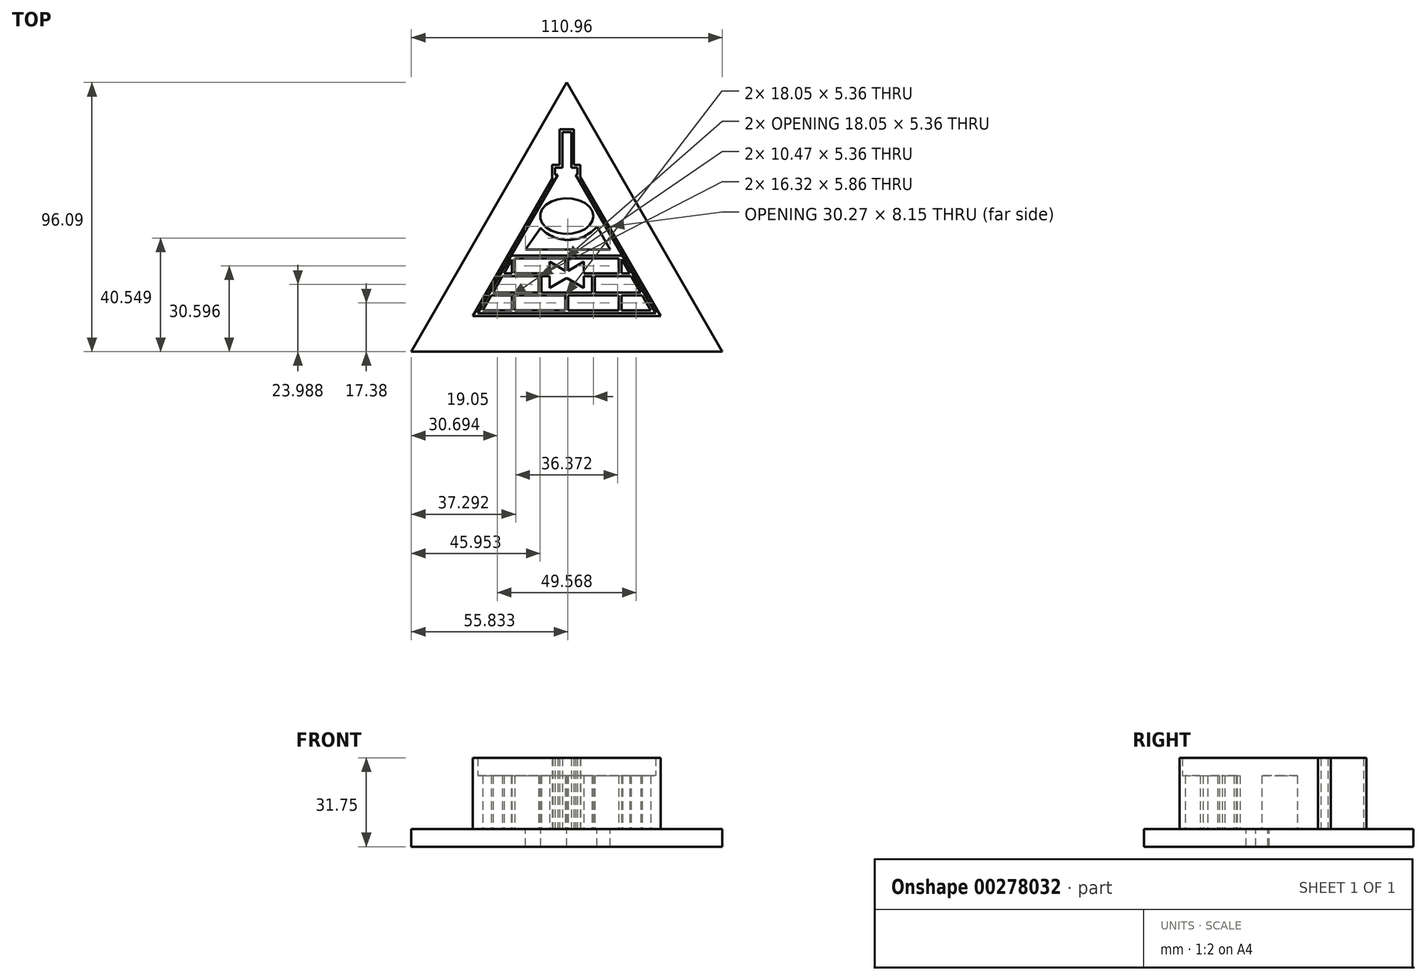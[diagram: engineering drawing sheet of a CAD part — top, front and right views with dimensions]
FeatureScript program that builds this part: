
annotation { "Feature Type Name" : "Feature", "Feature Type Description" : "" }
export const myFeature = defineFeature(function(context is Context, id is Id, definition is map)
    precondition{}
    {
        {
            var Q0;
            Q0=qCreatedBy(makeId("Top.planeOp"),FACE);
            var sketch = newSketch(context, id + "F0", { "sketchPlane" : qUnion([Q0])});
            skLineSegment(sketch, "E0", {"start": v(-57.59, 40.25) * mm, "end": v(-86.1, -9.14) * mm});
            skLineSegment(sketch, "E1", {"start": v(-86.1, -9.14) * mm, "end": v(-22.6, -9.14) * mm});
            skLineSegment(sketch, "E2", {"start": v(-22.6, -9.14) * mm, "end": v(-51.12, 40.25) * mm});
            skEllipse(sketch, "E3", {"center": v(-54.35, 25.53) * mm, "majorRadius": 6.35 * mm, "minorRadius": 9.53 * mm, "majorAxis": v(0, -1)});
            skPoint(sketch, "E4.startSnap0", {"position": v(-63.88, 25.53) * mm});
            skPoint(sketch, "E4.endSnap0", {"position": v(-63.88, 25.53) * mm});
            skLineSegment(sketch, "E5", {"start": v(-74.22, 11.44) * mm, "end": v(-34.48, 11.44) * mm});
            skLineSegment(sketch, "E6", {"start": v(-30.52, 4.58) * mm, "end": v(-49.3, 4.58) * mm});
            skLineSegment(sketch, "E7", {"start": v(-82.14, -2.28) * mm, "end": v(-26.56, -2.28) * mm});
            skLineSegment(sketch, "E8", {"start": v(-73.4, 11.44) * mm, "end": v(-73.4, 4.58) * mm});
            skLineSegment(sketch, "E9", {"start": v(-35.3, 11.44) * mm, "end": v(-35.3, 4.58) * mm});
            skLineSegment(sketch, "E10", {"start": v(-63.88, 4.58) * mm, "end": v(-63.88, -2.28) * mm});
            skLineSegment(sketch, "E11", {"start": v(-44.83, 4.58) * mm, "end": v(-44.83, -2.28) * mm});
            skLineSegment(sketch, "E12.trimOffspring", {"start": v(-35.3, -2.28) * mm, "end": v(-35.3, -9.14) * mm});
            skLineSegment(sketch, "E13.trimOffspring", {"start": v(-54.35, -2.28) * mm, "end": v(-54.35, -9.14) * mm});
            skLineSegment(sketch, "E14.bottom", {"start": v(-54.35, 29.34) * mm, "end": v(-54.35, 29.34) * mm});
            skLineSegment(sketch, "E14.top", {"start": v(-54.35, 21.72) * mm, "end": v(-54.35, 21.72) * mm});
            skLineSegment(sketch, "E14.left", {"start": v(-54.86, 28.84) * mm, "end": v(-54.86, 22.23) * mm});
            skLineSegment(sketch, "E14.right", {"start": v(-53.84, 28.84) * mm, "end": v(-53.84, 22.23) * mm});
            skPoint(sketch, "E15.visualSharp", {"position": v(-54.86, 29.34) * mm});
            skArc(sketch, "E15.filletArc", {"start": v(-54.35, 29.34) * mm, "mid": v(-54.71, 29.2) * mm, "end": v(-54.86, 28.84) * mm});
            skPoint(sketch, "E16.visualSharp", {"position": v(-53.84, 29.34) * mm});
            skArc(sketch, "E16.filletArc", {"start": v(-53.84, 28.84) * mm, "mid": v(-54, 29.2) * mm, "end": v(-54.35, 29.34) * mm});
            skPoint(sketch, "E17.visualSharp", {"position": v(-54.86, 21.72) * mm});
            skArc(sketch, "E17.filletArc", {"start": v(-54.86, 22.23) * mm, "mid": v(-54.71, 21.87) * mm, "end": v(-54.35, 21.72) * mm});
            skPoint(sketch, "E18.visualSharp", {"position": v(-53.84, 21.72) * mm});
            skArc(sketch, "E18.filletArc", {"start": v(-54.35, 21.72) * mm, "mid": v(-54, 21.87) * mm, "end": v(-53.84, 22.23) * mm});
            skLineSegment(sketch, "E19.trimOffspring", {"start": v(-59.41, 4.58) * mm, "end": v(-78.18, 4.58) * mm});
            skLineSegment(sketch, "E20.bottom", {"start": v(-58.55, 40.25) * mm, "end": v(-57.59, 40.25) * mm});
            skLineSegment(sketch, "E20.top", {"start": v(-58.55, 42.8) * mm, "end": v(-55.94, 42.8) * mm});
            skLineSegment(sketch, "E20.left", {"start": v(-58.55, 40.25) * mm, "end": v(-58.55, 42.8) * mm});
            skLineSegment(sketch, "E20.right", {"start": v(-50.54, 40.25) * mm, "end": v(-50.54, 42.8) * mm});
            skLineSegment(sketch, "E21.top", {"start": v(-55.94, 55.5) * mm, "end": v(-52.76, 55.5) * mm});
            skLineSegment(sketch, "E21.left", {"start": v(-55.94, 42.8) * mm, "end": v(-55.94, 55.5) * mm});
            skLineSegment(sketch, "E21.right", {"start": v(-52.76, 42.8) * mm, "end": v(-52.76, 55.5) * mm});
            skPoint(sketch, "E22.orphan", {"position": v(-54.35, 45.85) * mm});
            skPoint(sketch, "E4.start.orphan", {"position": v(-42.62, 25.53) * mm});
            skPoint(sketch, "E23.trimOffspring.end.orphan", {"position": v(-66.08, 25.53) * mm});
            skLineSegment(sketch, "E24.trimOffspring", {"start": v(-51.12, 40.25) * mm, "end": v(-50.54, 40.25) * mm});
            skLineSegment(sketch, "E25.trimOffspring", {"start": v(-52.76, 42.8) * mm, "end": v(-50.54, 42.8) * mm});
            skLineSegment(sketch, "E26.0", {"start": v(-59.55, 43.8) * mm, "end": v(-56.94, 43.8) * mm});
            skLineSegment(sketch, "E26.1", {"start": v(-49.54, 39.25) * mm, "end": v(-49.54, 43.8) * mm});
            skLineSegment(sketch, "E26.2", {"start": v(-51.76, 43.8) * mm, "end": v(-49.54, 43.8) * mm});
            skLineSegment(sketch, "E26.3", {"start": v(-51.76, 43.8) * mm, "end": v(-51.76, 56.5) * mm});
            skLineSegment(sketch, "E26.4", {"start": v(-56.94, 56.5) * mm, "end": v(-51.76, 56.5) * mm});
            skLineSegment(sketch, "E26.5", {"start": v(-49.54, 39.25) * mm, "end": v(-49.39, 39.25) * mm});
            skLineSegment(sketch, "E26.6", {"start": v(-56.94, 43.8) * mm, "end": v(-56.94, 56.5) * mm});
            skLineSegment(sketch, "E26.7", {"start": v(-20.87, -10.14) * mm, "end": v(-49.39, 39.25) * mm});
            skLineSegment(sketch, "E26.8", {"start": v(-87.83, -10.14) * mm, "end": v(-20.87, -10.14) * mm});
            skLineSegment(sketch, "E26.9", {"start": v(-59.32, 39.25) * mm, "end": v(-87.83, -10.14) * mm});
            skLineSegment(sketch, "E26.10", {"start": v(-59.55, 39.25) * mm, "end": v(-59.32, 39.25) * mm});
            skLineSegment(sketch, "E26.11", {"start": v(-59.55, 39.25) * mm, "end": v(-59.55, 43.8) * mm});
            skLineSegment(sketch, "E27", {"start": v(-81.28, -2.78) * mm, "end": v(-73.9, -2.78) * mm});
            skLineSegment(sketch, "E28", {"start": v(-27.43, -2.78) * mm, "end": v(-24.33, -8.14) * mm});
            skLineSegment(sketch, "E29", {"start": v(-24.33, -8.14) * mm, "end": v(-34.8, -8.14) * mm});
            skLineSegment(sketch, "E30", {"start": v(-84.37, -8.14) * mm, "end": v(-81.28, -2.78) * mm});
            skLineSegment(sketch, "E31", {"start": v(-73.9, -2.78) * mm, "end": v(-73.9, -8.14) * mm});
            skLineSegment(sketch, "E32", {"start": v(-72.9, -2.78) * mm, "end": v(-72.9, -8.14) * mm});
            skLineSegment(sketch, "E33", {"start": v(-54.85, -2.78) * mm, "end": v(-54.85, -8.14) * mm});
            skLineSegment(sketch, "E34", {"start": v(-53.85, -2.78) * mm, "end": v(-53.85, -8.14) * mm});
            skLineSegment(sketch, "E35", {"start": v(-35.8, -2.78) * mm, "end": v(-35.8, -8.14) * mm});
            skLineSegment(sketch, "E36", {"start": v(-34.8, -2.78) * mm, "end": v(-34.8, -8.14) * mm});
            skLineSegment(sketch, "E37.trimOffspring", {"start": v(-72.9, -2.78) * mm, "end": v(-54.85, -2.78) * mm});
            skLineSegment(sketch, "E38.trimOffspring", {"start": v(-73.9, -8.14) * mm, "end": v(-84.37, -8.14) * mm});
            skPoint(sketch, "E39.trimOffspring.end.orphan", {"position": v(-73.4, -9.14) * mm});
            skPoint(sketch, "E39.trimOffspring.start.orphan", {"position": v(-73.4, -2.28) * mm});
            skLineSegment(sketch, "E40", {"start": v(-73.4, -2.28) * mm, "end": v(-73.4, -9.14) * mm});
            skLineSegment(sketch, "E41.trimOffspring", {"start": v(-53.85, -2.78) * mm, "end": v(-35.8, -2.78) * mm});
            skLineSegment(sketch, "E42.trimOffspring", {"start": v(-54.85, -8.14) * mm, "end": v(-72.9, -8.14) * mm});
            skLineSegment(sketch, "E43.trimOffspring", {"start": v(-34.8, -2.78) * mm, "end": v(-27.43, -2.78) * mm});
            skLineSegment(sketch, "E44.trimOffspring", {"start": v(-35.8, -8.14) * mm, "end": v(-53.85, -8.14) * mm});
            skLineSegment(sketch, "E45", {"start": v(-80.7, -1.78) * mm, "end": v(-64.38, -1.78) * mm});
            skLineSegment(sketch, "E46", {"start": v(-28, -1.78) * mm, "end": v(-31.39, 4.08) * mm});
            skLineSegment(sketch, "E47", {"start": v(-31.39, 4.08) * mm, "end": v(-44.33, 4.08) * mm});
            skLineSegment(sketch, "E48", {"start": v(-48.3, 4.08) * mm, "end": v(-48.3, -0.08) * mm});
            skLineSegment(sketch, "E49", {"start": v(-48.3, -0.08) * mm, "end": v(-54.35, 3.42) * mm});
            skLineSegment(sketch, "E50", {"start": v(-54.35, 3.42) * mm, "end": v(-60.41, -0.08) * mm});
            skLineSegment(sketch, "E51", {"start": v(-60.41, -0.08) * mm, "end": v(-60.41, 4.08) * mm});
            skLineSegment(sketch, "E52", {"start": v(-60.41, 4.08) * mm, "end": v(-63.38, 4.08) * mm});
            skLineSegment(sketch, "E53", {"start": v(-77.32, 4.08) * mm, "end": v(-80.7, -1.78) * mm});
            skLineSegment(sketch, "E54", {"start": v(-64.38, -1.78) * mm, "end": v(-64.38, 4.08) * mm});
            skLineSegment(sketch, "E55", {"start": v(-63.38, 4.08) * mm, "end": v(-63.38, -1.78) * mm});
            skLineSegment(sketch, "E56", {"start": v(-45.33, 4.08) * mm, "end": v(-45.33, -1.78) * mm});
            skLineSegment(sketch, "E57", {"start": v(-44.33, 4.08) * mm, "end": v(-44.33, -1.78) * mm});
            skLineSegment(sketch, "E58.trimOffspring", {"start": v(-64.38, 4.08) * mm, "end": v(-77.32, 4.08) * mm});
            skLineSegment(sketch, "E59.trimOffspring", {"start": v(-63.38, -1.78) * mm, "end": v(-45.33, -1.78) * mm});
            skLineSegment(sketch, "E60.trimOffspring", {"start": v(-44.33, -1.78) * mm, "end": v(-28, -1.78) * mm});
            skLineSegment(sketch, "E61.trimOffspring", {"start": v(-45.33, 4.08) * mm, "end": v(-48.3, 4.08) * mm});
            skLineSegment(sketch, "E62", {"start": v(-31.88, 5.08) * mm, "end": v(-34.8, 5.08) * mm});
            skLineSegment(sketch, "E63", {"start": v(-48.3, 5.08) * mm, "end": v(-48.3, 9.23) * mm});
            skLineSegment(sketch, "E64", {"start": v(-60.41, 5.08) * mm, "end": v(-72.9, 5.08) * mm});
            skLineSegment(sketch, "E65", {"start": v(-76.74, 5.08) * mm, "end": v(-73.9, 10) * mm});
            skLineSegment(sketch, "E66", {"start": v(-72.9, 10.44) * mm, "end": v(-54.85, 10.44) * mm});
            skLineSegment(sketch, "E67", {"start": v(-34.8, 10.14) * mm, "end": v(-31.88, 5.08) * mm});
            skLineSegment(sketch, "E68", {"start": v(-34.8, 5.08) * mm, "end": v(-34.8, 10.14) * mm});
            skLineSegment(sketch, "E69", {"start": v(-35.8, 10.44) * mm, "end": v(-35.8, 5.08) * mm});
            skLineSegment(sketch, "E70", {"start": v(-53.85, 6.02) * mm, "end": v(-53.85, 10.44) * mm});
            skLineSegment(sketch, "E71", {"start": v(-54.85, 10.44) * mm, "end": v(-54.85, 6.02) * mm});
            skLineSegment(sketch, "E72", {"start": v(-72.9, 10.44) * mm, "end": v(-72.9, 5.08) * mm});
            skLineSegment(sketch, "E73.trimOffspring", {"start": v(-35.8, 5.08) * mm, "end": v(-48.3, 5.08) * mm});
            skLineSegment(sketch, "E74.trimOffspring", {"start": v(-53.85, 10.44) * mm, "end": v(-35.8, 10.44) * mm});
            skLineSegment(sketch, "E75", {"start": v(-53.85, 6.02) * mm, "end": v(-48.3, 9.23) * mm});
            skLineSegment(sketch, "E76", {"start": v(-60.41, 5.08) * mm, "end": v(-60.41, 9.23) * mm});
            skLineSegment(sketch, "E77", {"start": v(-60.41, 9.23) * mm, "end": v(-54.85, 6.02) * mm});
            skLineSegment(sketch, "E78", {"start": v(-73.9, 10) * mm, "end": v(-73.9, 5.08) * mm});
            skLineSegment(sketch, "E79.trimOffspring", {"start": v(-73.9, 5.08) * mm, "end": v(-76.74, 5.08) * mm});
            skFitSpline(sketch, "E80.0", {"points": [v(-45.92, 24.58) * mm, v(-45.78, 25.53) * mm, v(-45.92, 26.49) * mm, v(-46.35, 27.44) * mm, v(-47.1, 28.37) * mm, v(-48.13, 29.21) * mm, v(-49.43, 29.93) * mm, v(-50.95, 30.47) * mm, v(-52.33, 30.75) * mm, v(-53.48, 30.86) * mm, v(-54.35, 30.9) * mm, v(-55.23, 30.86) * mm, v(-56.37, 30.75) * mm, v(-57.75, 30.47) * mm, v(-59.28, 29.93) * mm, v(-60.58, 29.21) * mm, v(-61.61, 28.37) * mm, v(-62.36, 27.44) * mm, v(-62.78, 26.49) * mm, v(-62.92, 25.53) * mm, v(-62.78, 24.58) * mm, v(-62.36, 23.63) * mm, v(-61.61, 22.7) * mm, v(-60.58, 21.85) * mm, v(-59.28, 21.14) * mm, v(-57.75, 20.6) * mm, v(-56.37, 20.32) * mm, v(-55.23, 20.2) * mm, v(-54.35, 20.17) * mm, v(-53.48, 20.2) * mm, v(-52.33, 20.32) * mm, v(-50.95, 20.6) * mm, v(-49.43, 21.14) * mm, v(-48.13, 21.85) * mm, v(-47.1, 22.7) * mm, v(-46.35, 23.63) * mm, v(-45.92, 24.58) * mm, v(-45.78, 25.53) * mm, v(-45.92, 26.49) * mm, v(-45.92, 24.58) * mm]});
            skSolve(sketch);
        }
        {
            var Q0;
            {var subQ0=sQuery(id+"F0.wireOp",EDGE,"E10");Q0=makeQuery(id+"F0.imprint","IMPRINT",FACE,{"disambiguationData":[TD([[makeQuery(id+"F0.imprint","IMPRINT",EDGE,{"derivedFrom":subQ0}),-1.0]])]});}
            var Q1;
            Q1=makeQuery(id+"F0.imprint","IMPRINT",FACE,{"disambiguationData":[TD([[makeQuery(id+"F0.imprint","IMPRINT",EDGE,{"derivedFrom":sQuery(id+"F0.wireOp",EDGE,"E27")}),1.0]])]});
            var Q2;
            {var subQ0=sQuery(id+"F0.wireOp",EDGE,"E13.trimOffspring");Q2=makeQuery(id+"F0.imprint","IMPRINT",FACE,{"disambiguationData":[TD([[makeQuery(id+"F0.imprint","IMPRINT",EDGE,{"derivedFrom":subQ0}),-1.0]])]});}
            var Q3;
            {var subQ7=sQuery(id+"F0.wireOp",EDGE,"E8");Q3=makeQuery(id+"F0.imprint","IMPRINT",FACE,{"disambiguationData":[TD([[makeQuery(id+"F0.imprint","IMPRINT",EDGE,{"derivedFrom":subQ7}),1.0]])]});}
            var Q4;
            {var subQ1=sQuery(id+"F0.wireOp",EDGE,"E8");Q4=makeQuery(id+"F0.imprint","IMPRINT",FACE,{"disambiguationData":[TD([[makeQuery(id+"F0.imprint","IMPRINT",EDGE,{"derivedFrom":subQ1}),-1.0]])]});}
            var Q5;
            {var subQ3=sQuery(id+"F0.wireOp",EDGE,"E9");Q5=makeQuery(id+"F0.imprint","IMPRINT",FACE,{"disambiguationData":[TD([[makeQuery(id+"F0.imprint","IMPRINT",EDGE,{"derivedFrom":subQ3}),1.0]])]});}
            var Q6;
            {var subQ0=sQuery(id+"F0.wireOp",EDGE,"E11");Q6=makeQuery(id+"F0.imprint","IMPRINT",FACE,{"disambiguationData":[TD([[makeQuery(id+"F0.imprint","IMPRINT",EDGE,{"derivedFrom":subQ0}),1.0]])]});}
            var Q7;
            {var subQ0=sQuery(id+"F0.wireOp",EDGE,"E12.trimOffspring");Q7=makeQuery(id+"F0.imprint","IMPRINT",FACE,{"disambiguationData":[TD([[makeQuery(id+"F0.imprint","IMPRINT",EDGE,{"derivedFrom":subQ0}),1.0]])]});}
            var Q8;
            {var subQ0=sQuery(id+"F0.wireOp",EDGE,"E12.trimOffspring");Q8=makeQuery(id+"F0.imprint","IMPRINT",FACE,{"disambiguationData":[TD([[makeQuery(id+"F0.imprint","IMPRINT",EDGE,{"derivedFrom":subQ0}),-1.0]])]});}
            var Q9;
            Q9=makeQuery(id+"F0.imprint","IMPRINT",FACE,{"disambiguationData":[TD([[makeQuery(id+"F0.imprint","IMPRINT",EDGE,{"derivedFrom":sQuery(id+"F0.wireOp",EDGE,"E3")}),1.0]])]});
            var Q10;
            Q10=makeQuery(id+"F0.imprint","IMPRINT",FACE,{"disambiguationData":[TD([[makeQuery(id+"F0.imprint","IMPRINT",EDGE,{"derivedFrom":sQuery(id+"F0.wireOp",EDGE,"E14.left")}),1.0]])]});
            extrude(context, id + "F1", {"entities" : qUnion([Q0, Q1, Q2, Q3, Q4, Q5, Q6, Q7, Q8, Q9, Q10]), "depth" : 19.05 * mm});
        }
        {
            var Q0;
            {var subQ1=sQuery(id+"F0.wireOp",EDGE,"E20.bottom");Q0=makeQuery(id+"F0.imprint","IMPRINT",FACE,{"disambiguationData":[TD([[makeQuery(id+"F0.imprint","IMPRINT",EDGE,{"derivedFrom":subQ1}),-1.0]])]});}
            extrude(context, id + "F2", {"entities" : qUnion([Q0]), "operationType" : NewBodyOperationType.ADD, "depth" : 25.4 * mm});
        }
        {
            var Q0;
            {var subQ1=sQuery(id+"F0.wireOp",EDGE,"E20.bottom");Q0=makeQuery(id+"F0.imprint","IMPRINT",FACE,{"disambiguationData":[TD([[makeQuery(id+"F0.imprint","IMPRINT",EDGE,{"derivedFrom":subQ1}),-1.0]])]});}
            var sketch = newSketch(context, id + "F3", { "sketchPlane" : qUnion([Q0])});
            skLineSegment(sketch, "E81", {"start": v(1.13, -22.84) * mm, "end": v(-54.35, 73.25) * mm});
            skLineSegment(sketch, "E82", {"start": v(-54.35, 73.25) * mm, "end": v(-109.83, -22.84) * mm});
            skLineSegment(sketch, "E83", {"start": v(-109.83, -22.84) * mm, "end": v(1.13, -22.84) * mm});
            skLineSegment(sketch, "E84", {"start": v(-43.6, 21.79) * mm, "end": v(-38.86, 13.63) * mm});
            skLineSegment(sketch, "E85", {"start": v(-38.86, 13.63) * mm, "end": v(-69.13, 13.63) * mm});
            skLineSegment(sketch, "E86", {"start": v(-69.13, 13.63) * mm, "end": v(-63.69, 21.33) * mm});
            skArc(sketch, "E87", {"start": v(-63.69, 21.33) * mm, "mid": v(-53.54, 17.02) * mm, "end": v(-43.6, 21.79) * mm});
            skSolve(sketch);
        }
        {
            var Q0;
            Q0=makeQuery(id+"F3.imprint","IMPRINT",FACE,{"disambiguationData":[TD([[makeQuery(id+"F3.imprint","IMPRINT",EDGE,{"derivedFrom":sQuery(id+"F3.wireOp",EDGE,"E84")}),1.0]])]});
            var Q1;
            {var subQ1=sQuery(id+"F0.wireOp",EDGE,"E20.bottom");Q1=makeQuery(id+"F3.imprint","IMPRINT",FACE,{"disambiguationData":[TD([[makeQuery(id+"F3.imprint","IMPRINT",EDGE,{"derivedFrom":makeQuery(id+"F0.imprint","IMPRINT",EDGE,{"derivedFrom":subQ1})}),-1.0]])]});}
            var Q2;
            Q2=makeQuery(id+"F3.imprint","IMPRINT",FACE,{"disambiguationData":[TD([[makeQuery(id+"F3.imprint","IMPRINT",EDGE,{"derivedFrom":sQuery(id+"F3.wireOp",EDGE,"E81")}),1.0]])]});
            extrude(context, id + "F4", {"entities" : qUnion([Q0, Q1, Q2]), "oppositeDirection" : true, "depth" : 6.35 * mm});
        }
    });
